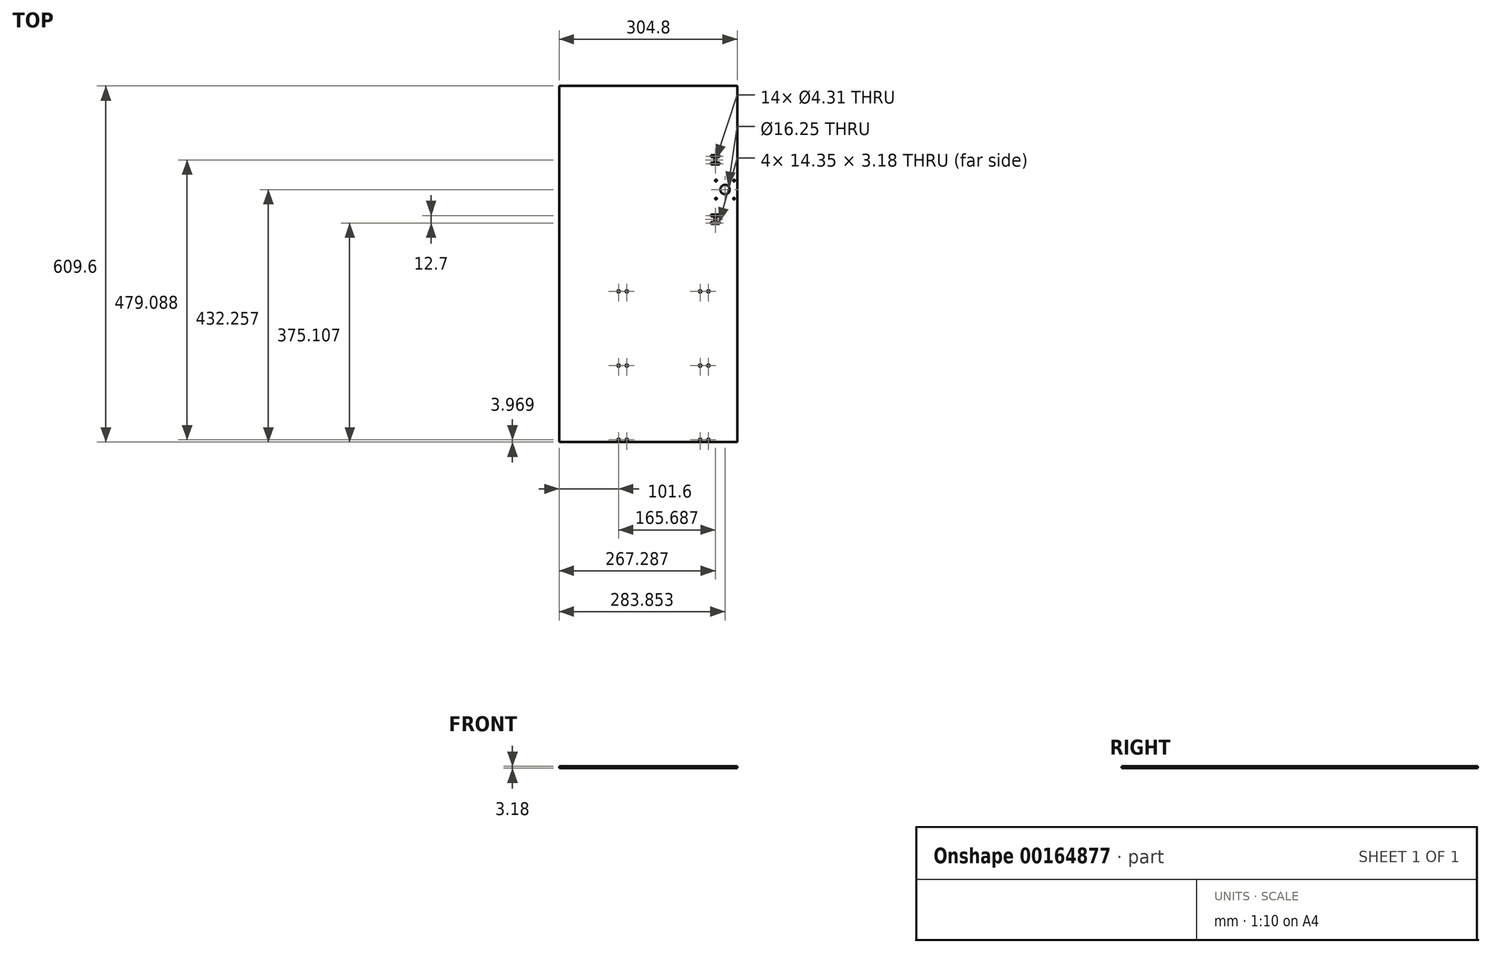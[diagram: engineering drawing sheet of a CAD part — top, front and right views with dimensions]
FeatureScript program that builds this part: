
annotation { "Feature Type Name" : "Feature", "Feature Type Description" : "" }
export const myFeature = defineFeature(function(context is Context, id is Id, definition is map)
    precondition{}
    {
        {
            var Q0;
            Q0=qCreatedBy(makeId("Top.planeOp"),FACE);
            var sketch = newSketch(context, id + "F0", { "sketchPlane" : qUnion([Q0])});
            skLineSegment(sketch, "E0.bottom", {"start": v(0, 0) * mm, "end": v(304.8, 0) * mm});
            skLineSegment(sketch, "E0.top", {"start": v(0, 609.6) * mm, "end": v(304.8, 609.6) * mm});
            skLineSegment(sketch, "E0.left", {"start": v(0, 0) * mm, "end": v(0, 609.6) * mm});
            skLineSegment(sketch, "E0.right", {"start": v(304.8, 0) * mm, "end": v(304.8, 609.6) * mm});
            skLineSegment(sketch, "E1", {"start": v(178.6, 0) * mm, "end": v(178.6, 3.97) * mm, "construction": true});
            skLineSegment(sketch, "E2", {"start": v(101.6, 3.97) * mm, "end": v(115.89, 3.97) * mm, "construction": true});
            skLineSegment(sketch, "E3", {"start": v(115.89, 3.97) * mm, "end": v(241.3, 3.97) * mm, "construction": true});
            skLineSegment(sketch, "E4", {"start": v(241.3, 3.97) * mm, "end": v(255.59, 3.97) * mm, "construction": true});
            skLineSegment(sketch, "E5", {"start": v(178.6, 3.97) * mm, "end": v(178.6, 130.97) * mm, "construction": true});
            skLineSegment(sketch, "E6", {"start": v(101.6, 130.97) * mm, "end": v(115.89, 130.97) * mm, "construction": true});
            skLineSegment(sketch, "E7", {"start": v(115.89, 130.97) * mm, "end": v(241.3, 130.97) * mm, "construction": true});
            skLineSegment(sketch, "E8", {"start": v(241.3, 130.97) * mm, "end": v(255.59, 130.97) * mm, "construction": true});
            skLineSegment(sketch, "E9", {"start": v(101.6, 3.97) * mm, "end": v(0, 3.97) * mm, "construction": true});
            skLineSegment(sketch, "E10", {"start": v(178.6, 130.97) * mm, "end": v(178.6, 257.97) * mm, "construction": true});
            skLineSegment(sketch, "E11", {"start": v(101.6, 257.97) * mm, "end": v(115.89, 257.97) * mm, "construction": true});
            skLineSegment(sketch, "E12", {"start": v(115.89, 257.97) * mm, "end": v(241.3, 257.97) * mm, "construction": true});
            skLineSegment(sketch, "E13", {"start": v(241.3, 257.97) * mm, "end": v(255.59, 257.97) * mm, "construction": true});
            skCircle(sketch, "E14", {"center": v(115.89, 3.97) * mm, "radius": 2.15 * mm});
            skCircle(sketch, "E15", {"center": v(101.6, 3.97) * mm, "radius": 2.15 * mm});
            skCircle(sketch, "E16", {"center": v(241.3, 3.97) * mm, "radius": 2.15 * mm});
            skCircle(sketch, "E17", {"center": v(255.59, 3.97) * mm, "radius": 2.15 * mm});
            skCircle(sketch, "E18", {"center": v(241.3, 130.97) * mm, "radius": 2.15 * mm});
            skCircle(sketch, "E19", {"center": v(255.59, 130.97) * mm, "radius": 2.15 * mm});
            skCircle(sketch, "E20", {"center": v(115.89, 130.97) * mm, "radius": 2.15 * mm});
            skCircle(sketch, "E21", {"center": v(101.6, 130.97) * mm, "radius": 2.15 * mm});
            skCircle(sketch, "E22", {"center": v(241.3, 257.97) * mm, "radius": 2.15 * mm});
            skCircle(sketch, "E23", {"center": v(255.59, 257.97) * mm, "radius": 2.15 * mm});
            skCircle(sketch, "E24", {"center": v(115.89, 257.97) * mm, "radius": 2.15 * mm});
            skCircle(sketch, "E25", {"center": v(101.6, 257.97) * mm, "radius": 2.15 * mm});
            skLineSegment(sketch, "E26", {"start": v(304.8, 432.26) * mm, "end": v(283.85, 432.26) * mm, "construction": true});
            skLineSegment(sketch, "E27.bottom", {"start": v(268.35, 416.76) * mm, "end": v(299.35, 416.76) * mm, "construction": true});
            skLineSegment(sketch, "E27.top", {"start": v(268.35, 447.76) * mm, "end": v(299.35, 447.76) * mm, "construction": true});
            skLineSegment(sketch, "E27.left", {"start": v(268.35, 416.76) * mm, "end": v(268.35, 447.76) * mm, "construction": true});
            skLineSegment(sketch, "E27.right", {"start": v(299.35, 416.76) * mm, "end": v(299.35, 447.76) * mm, "construction": true});
            skPoint(sketch, "E27.middle", {"position": v(283.85, 432.26) * mm});
            skCircle(sketch, "E28", {"center": v(299.35, 447.76) * mm, "radius": 1.5 * mm});
            skCircle(sketch, "E29", {"center": v(268.35, 447.76) * mm, "radius": 1.5 * mm});
            skCircle(sketch, "E30", {"center": v(268.35, 416.76) * mm, "radius": 1.5 * mm});
            skCircle(sketch, "E31", {"center": v(299.35, 416.76) * mm, "radius": 1.5 * mm});
            skCircle(sketch, "E32", {"center": v(283.85, 432.26) * mm, "radius": 8.13 * mm});
            skLineSegment(sketch, "E33", {"start": v(283.85, 432.26) * mm, "end": v(267.29, 432.26) * mm, "construction": true});
            skLineSegment(sketch, "E34.bottom", {"start": v(274.46, 491) * mm, "end": v(260.11, 491) * mm});
            skLineSegment(sketch, "E34.top", {"start": v(274.46, 487.82) * mm, "end": v(260.11, 487.82) * mm});
            skLineSegment(sketch, "E34.left", {"start": v(274.46, 491) * mm, "end": v(274.46, 487.82) * mm});
            skLineSegment(sketch, "E34.right", {"start": v(260.11, 491) * mm, "end": v(260.11, 487.82) * mm});
            skLineSegment(sketch, "E35.bottom", {"start": v(274.46, 478.3) * mm, "end": v(260.11, 478.3) * mm});
            skLineSegment(sketch, "E35.top", {"start": v(274.46, 475.12) * mm, "end": v(260.11, 475.12) * mm});
            skLineSegment(sketch, "E35.left", {"start": v(274.46, 478.3) * mm, "end": v(274.46, 475.12) * mm});
            skLineSegment(sketch, "E35.right", {"start": v(260.11, 478.3) * mm, "end": v(260.11, 475.12) * mm});
            skLineSegment(sketch, "E36.bottom", {"start": v(274.46, 389.4) * mm, "end": v(260.11, 389.4) * mm});
            skLineSegment(sketch, "E36.top", {"start": v(274.46, 386.22) * mm, "end": v(260.11, 386.22) * mm});
            skLineSegment(sketch, "E36.left", {"start": v(274.46, 389.4) * mm, "end": v(274.46, 386.22) * mm});
            skLineSegment(sketch, "E36.right", {"start": v(260.11, 389.4) * mm, "end": v(260.11, 386.22) * mm});
            skLineSegment(sketch, "E37.bottom", {"start": v(274.46, 376.7) * mm, "end": v(260.11, 376.7) * mm});
            skLineSegment(sketch, "E37.top", {"start": v(274.46, 373.52) * mm, "end": v(260.11, 373.52) * mm});
            skLineSegment(sketch, "E37.left", {"start": v(274.46, 376.7) * mm, "end": v(274.46, 373.52) * mm});
            skLineSegment(sketch, "E37.right", {"start": v(260.11, 376.7) * mm, "end": v(260.11, 373.52) * mm});
            skLineSegment(sketch, "E38", {"start": v(267.29, 487.82) * mm, "end": v(267.29, 478.3) * mm, "construction": true});
            skLineSegment(sketch, "E39", {"start": v(267.29, 475.12) * mm, "end": v(267.29, 389.4) * mm, "construction": true});
            skLineSegment(sketch, "E40", {"start": v(267.29, 386.22) * mm, "end": v(267.29, 376.7) * mm, "construction": true});
            skCircle(sketch, "E41", {"center": v(267.29, 483.06) * mm, "radius": 2.15 * mm});
            skCircle(sketch, "E42", {"center": v(267.29, 381.46) * mm, "radius": 2.15 * mm});
            skPoint(sketch, "E43", {"position": v(248.44, 3.97) * mm});
            skPoint(sketch, "E44", {"position": v(108.74, 3.97) * mm});
            skSolve(sketch);
        }
        {
            var Q0;
            Q0 = qSketchRegion(id + "F0", true);
            extrude(context, id + "F1", {"entities" : qUnion([Q0]), "depth" : 3.17 * mm});
        }
    });
